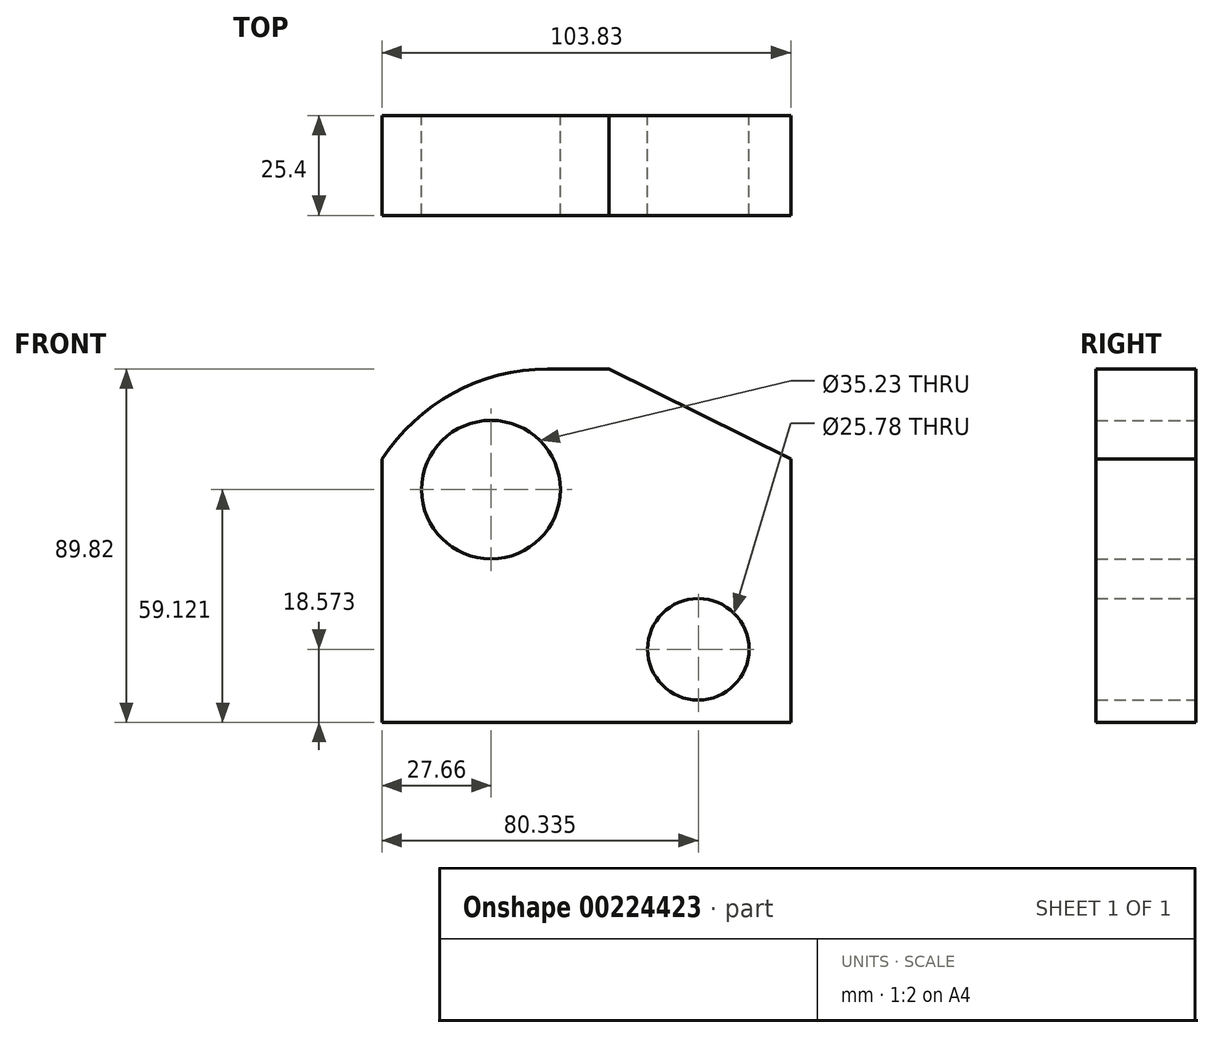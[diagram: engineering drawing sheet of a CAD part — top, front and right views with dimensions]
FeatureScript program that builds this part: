
annotation { "Feature Type Name" : "Feature", "Feature Type Description" : "" }
export const myFeature = defineFeature(function(context is Context, id is Id, definition is map)
    precondition{}
    {
        {
            var Q0;
            Q0=qCreatedBy(makeId("Front.planeOp"),FACE);
            var sketch = newSketch(context, id + "F0", { "sketchPlane" : qUnion([Q0])});
            skLineSegment(sketch, "E0", {"start": v(-64.04, 0) * mm, "end": v(-64.04, -66.89) * mm});
            skLineSegment(sketch, "E1", {"start": v(-64.04, -66.89) * mm, "end": v(39.8, -66.89) * mm});
            skLineSegment(sketch, "E2", {"start": v(39.8, 0) * mm, "end": v(39.8, -66.89) * mm});
            skLineSegment(sketch, "E3", {"start": v(39.8, 0) * mm, "end": v(-6.44, 22.93) * mm});
            skLineSegment(sketch, "E4", {"start": v(-21.98, 22.93) * mm, "end": v(-6.44, 22.93) * mm});
            skArc(sketch, "E5", {"start": v(-21.98, 22.93) * mm, "mid": v(-45.93, 16.82) * mm, "end": v(-64.04, 0) * mm});
            skCircle(sketch, "E6", {"center": v(-36.38, -7.77) * mm, "radius": 17.62 * mm});
            skCircle(sketch, "E7", {"center": v(16.3, -48.32) * mm, "radius": 12.9 * mm});
            skSolve(sketch);
        }
        {
            var Q0;
            Q0 = qSketchRegion(id + "F0", true);
            extrude(context, id + "F1", {"entities" : qUnion([Q0]), "depth" : 25.4 * mm});
        }
    });
